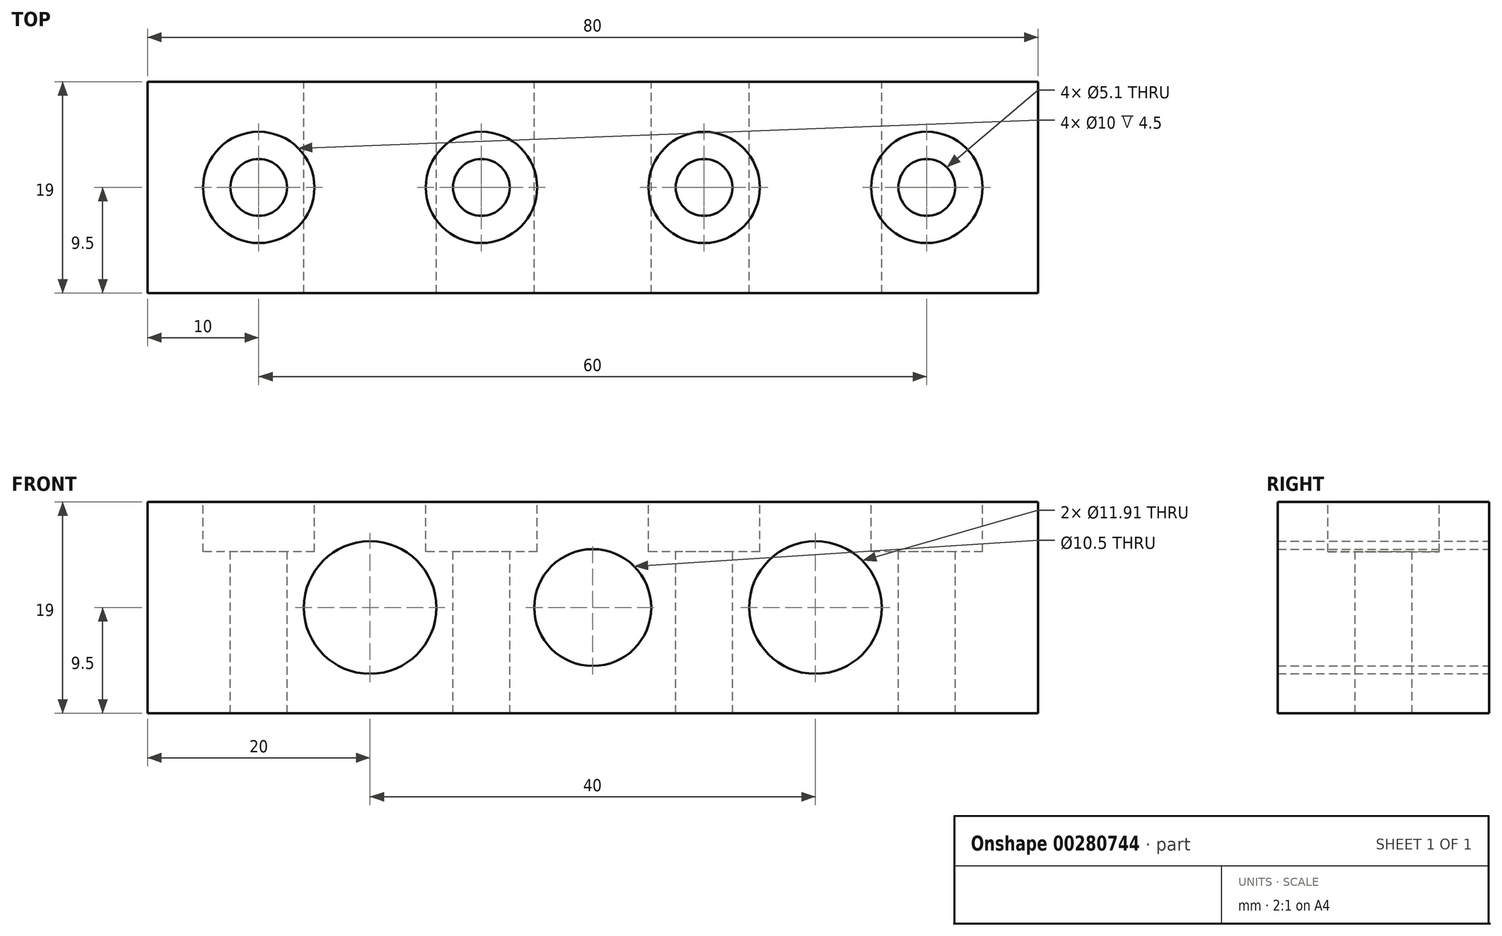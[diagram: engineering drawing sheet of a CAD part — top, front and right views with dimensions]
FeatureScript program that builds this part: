
annotation { "Feature Type Name" : "Feature", "Feature Type Description" : "" }
export const myFeature = defineFeature(function(context is Context, id is Id, definition is map)
    precondition{}
    {
        {
            var Q0;
            Q0=qCreatedBy(makeId("Top.planeOp"),FACE);
            var sketch = newSketch(context, id + "F0", { "sketchPlane" : qUnion([Q0])});
            skLineSegment(sketch, "E0.bottom", {"start": v(40, -9.5) * mm, "end": v(-40, -9.5) * mm});
            skLineSegment(sketch, "E0.top", {"start": v(40, 9.5) * mm, "end": v(-40, 9.5) * mm});
            skLineSegment(sketch, "E0.left", {"start": v(40, -9.5) * mm, "end": v(40, 9.5) * mm});
            skLineSegment(sketch, "E0.right", {"start": v(-40, -9.5) * mm, "end": v(-40, 9.5) * mm});
            skPoint(sketch, "E0.middle", {"position": v(0, 0) * mm});
            skSolve(sketch);
        }
        {
            var Q0;
            Q0=makeQuery(id+"F0.imprint","IMPRINT",FACE,{"disambiguationData":[TD([[makeQuery(id+"F0.imprint","IMPRINT",EDGE,{"derivedFrom":sQuery(id+"F0.wireOp",EDGE,"E0.bottom")}),-1.0]])]});
            extrude(context, id + "F1", {"entities" : qUnion([Q0]), "depth" : 19 * mm});
        }
        {
            var Q0;
            Q0=makeQuery(id+"F1.opExtrude","SWEPT_FACE",FACE,{"disambiguationData":[OSD([sQuery(id+"F0.wireOp",EDGE,"E0.top")])]});
            var sketch = newSketch(context, id + "F2", { "sketchPlane" : qUnion([Q0])});
            skLineSegment(sketch, "E1", {"start": v(-40, 9.5) * mm, "end": v(40, 9.5) * mm, "construction": true});
            skLineSegment(sketch, "E2", {"start": v(-30, 19) * mm, "end": v(-30, 0) * mm, "construction": true});
            skLineSegment(sketch, "E3", {"start": v(-10, 19) * mm, "end": v(-10, 0) * mm, "construction": true});
            skLineSegment(sketch, "E4", {"start": v(10, 19) * mm, "end": v(10, 0) * mm, "construction": true});
            skLineSegment(sketch, "E5", {"start": v(30, 19) * mm, "end": v(30, 0) * mm, "construction": true});
            skLineSegment(sketch, "E6", {"start": v(10, 19) * mm, "end": v(30, 0) * mm, "construction": true});
            skLineSegment(sketch, "E7", {"start": v(-10, 19) * mm, "end": v(-30, 0) * mm, "construction": true});
            skCircle(sketch, "E8", {"center": v(-20, 9.5) * mm, "radius": 5.96 * mm});
            skCircle(sketch, "E9", {"center": v(20, 9.5) * mm, "radius": 5.96 * mm});
            skCircle(sketch, "E10", {"center": v(0, 9.5) * mm, "radius": 5.25 * mm});
            skSolve(sketch);
        }
        {
            var Q0;
            Q0=makeQuery(id+"F2.imprint","IMPRINT",FACE,{"disambiguationData":[TD([[makeQuery(id+"F2.imprint","IMPRINT",EDGE,{"derivedFrom":sQuery(id+"F2.wireOp",EDGE,"E9")}),1.0]])]});
            var Q1;
            Q1=makeQuery(id+"F2.imprint","IMPRINT",FACE,{"disambiguationData":[TD([[makeQuery(id+"F2.imprint","IMPRINT",EDGE,{"derivedFrom":sQuery(id+"F2.wireOp",EDGE,"E8")}),1.0]])]});
            var Q2;
            Q2=makeQuery(id+"F2.imprint","IMPRINT",FACE,{"disambiguationData":[TD([[makeQuery(id+"F2.imprint","IMPRINT",EDGE,{"derivedFrom":sQuery(id+"F2.wireOp",EDGE,"E10")}),1.0]])]});
            extrude(context, id + "F3", {"entities" : qUnion([Q0, Q1, Q2]), "operationType" : NewBodyOperationType.REMOVE, "endBound" : BoundingType.THROUGH_ALL, "oppositeDirection" : true, "depth" : 12 * mm});
        }
        {
            var Q0;
            Q0=makeQuery(id+"F1.opExtrude","CAP_FACE",FACE,{"disambiguationData":[OSD([sQuery(id+"F0.wireOp",EDGE,"E0.bottom"),sQuery(id+"F0.wireOp",EDGE,"E0.top"),sQuery(id+"F0.wireOp",EDGE,"E0.left"),sQuery(id+"F0.wireOp",EDGE,"E0.right")])],"isStart":false});
            var sketch = newSketch(context, id + "F4", { "sketchPlane" : qUnion([Q0])});
            skLineSegment(sketch, "E11", {"start": v(-40, 0) * mm, "end": v(40, 0) * mm});
            skCircle(sketch, "E12", {"center": v(-30, 0) * mm, "radius": 2.55 * mm});
            skCircle(sketch, "E13.1.0.0", {"center": v(-10, 0) * mm, "radius": 2.55 * mm});
            skCircle(sketch, "E13.2.0.0", {"center": v(10, 0) * mm, "radius": 2.55 * mm});
            skCircle(sketch, "E13.3.0.0", {"center": v(30, 0) * mm, "radius": 2.55 * mm});
            skLineSegment(sketch, "E13.direction1", {"start": v(-30, 0) * mm, "end": v(-10, 0) * mm, "construction": true});
            skSolve(sketch);
        }
        {
            var Q0;
            Q0 = qSketchRegion(id + "F4", true);
            extrude(context, id + "F5", {"entities" : qUnion([Q0]), "operationType" : NewBodyOperationType.REMOVE, "endBound" : BoundingType.THROUGH_ALL, "oppositeDirection" : true, "depth" : 25 * mm});
        }
        {
            var Q0;
            Q0=makeQuery(id+"F1.opExtrude","CAP_FACE",FACE,{"disambiguationData":[OSD([sQuery(id+"F0.wireOp",EDGE,"E0.bottom"),sQuery(id+"F0.wireOp",EDGE,"E0.top"),sQuery(id+"F0.wireOp",EDGE,"E0.left"),sQuery(id+"F0.wireOp",EDGE,"E0.right")])],"isStart":false});
            var sketch = newSketch(context, id + "F6", { "sketchPlane" : qUnion([Q0])});
            skCircle(sketch, "E14", {"center": v(-30, 0) * mm, "radius": 5 * mm});
            skCircle(sketch, "E15.1.0.0", {"center": v(-10, 0) * mm, "radius": 5 * mm});
            skCircle(sketch, "E15.2.0.0", {"center": v(10, 0) * mm, "radius": 5 * mm});
            skCircle(sketch, "E15.3.0.0", {"center": v(30, 0) * mm, "radius": 5 * mm});
            skLineSegment(sketch, "E15.direction1", {"start": v(-30, 0) * mm, "end": v(-10, 0) * mm, "construction": true});
            skSolve(sketch);
        }
        {
            var Q0;
            Q0 = qSketchRegion(id + "F6", true);
            extrude(context, id + "F7", {"entities" : qUnion([Q0]), "operationType" : NewBodyOperationType.REMOVE, "oppositeDirection" : true, "depth" : 4.5 * mm});
        }
    });
